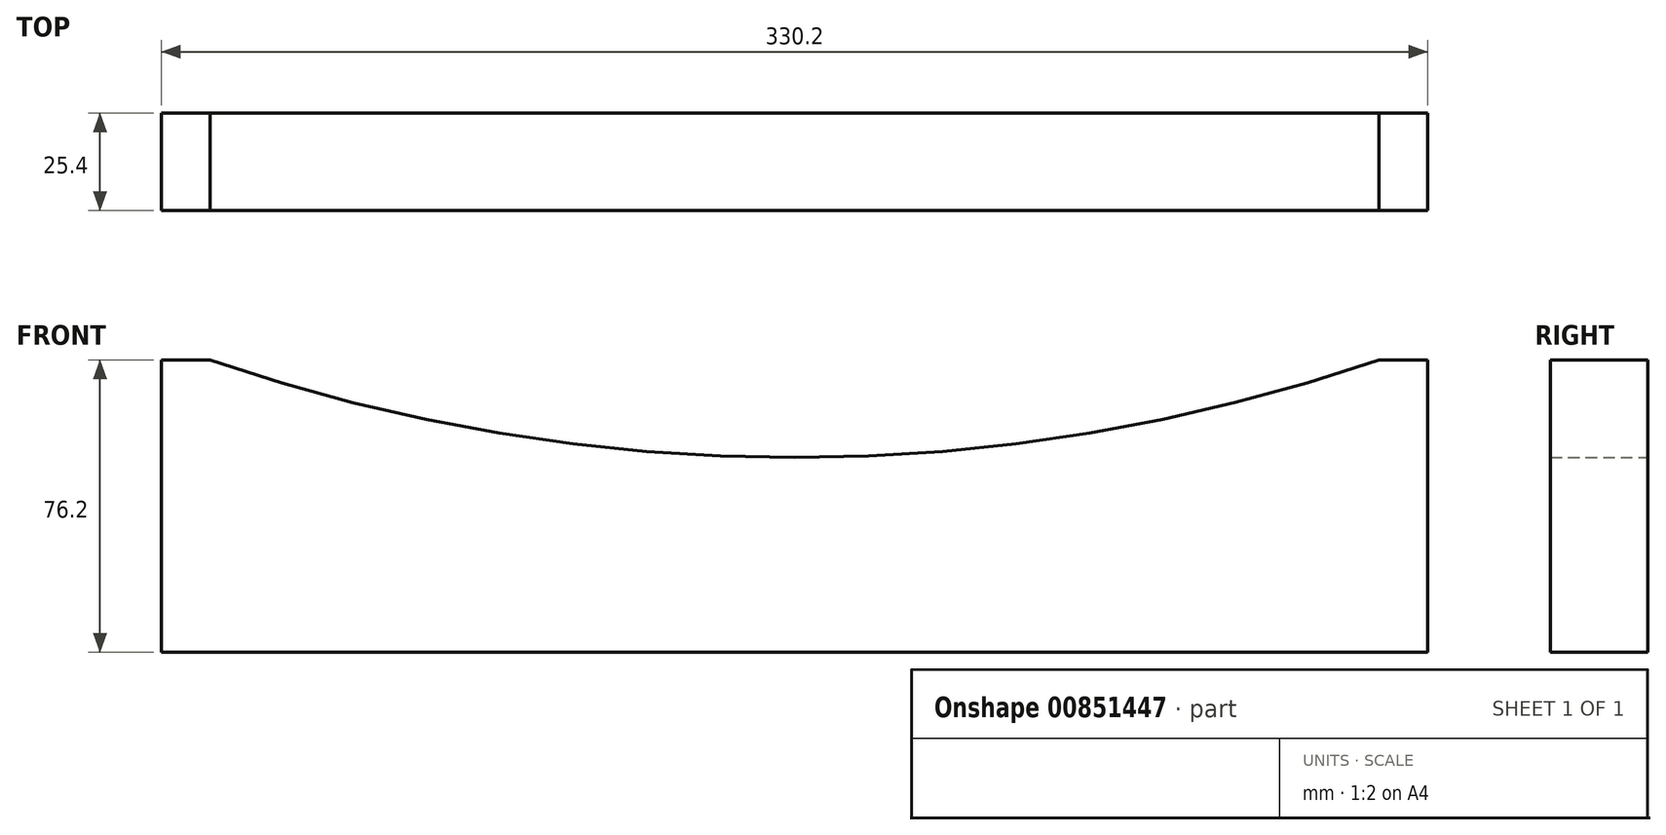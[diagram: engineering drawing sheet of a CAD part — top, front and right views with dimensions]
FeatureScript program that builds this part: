
annotation { "Feature Type Name" : "Feature", "Feature Type Description" : "" }
export const myFeature = defineFeature(function(context is Context, id is Id, definition is map)
    precondition{}
    {
        {
            var Q0;
            Q0=qCreatedBy(makeId("Front.planeOp"),FACE);
            var sketch = newSketch(context, id + "F0", { "sketchPlane" : qUnion([Q0])});
            skLineSegment(sketch, "E0.bottom", {"start": v(-152.21, 56.76) * mm, "end": v(-139.51, 56.76) * mm});
            skLineSegment(sketch, "E0.top", {"start": v(-152.21, -19.44) * mm, "end": v(177.99, -19.44) * mm});
            skLineSegment(sketch, "E0.left", {"start": v(-152.21, 56.76) * mm, "end": v(-152.21, -19.44) * mm});
            skLineSegment(sketch, "E0.right", {"start": v(177.99, 56.76) * mm, "end": v(177.99, -19.44) * mm});
            skArc(sketch, "E1", {"start": v(-139.51, 56.76) * mm, "mid": v(12.89, 31.36) * mm, "end": v(165.29, 56.76) * mm});
            skLineSegment(sketch, "E2.trimOffspring", {"start": v(165.29, 56.76) * mm, "end": v(177.99, 56.76) * mm});
            skSolve(sketch);
        }
        {
            var Q0;
            Q0=makeQuery(id+"F0.imprint","IMPRINT",FACE,{"disambiguationData":[TD([[makeQuery(id+"F0.imprint","IMPRINT",EDGE,{"derivedFrom":sQuery(id+"F0.wireOp",EDGE,"E0.bottom")}),-1.0]])]});
            extrude(context, id + "F1", {"entities" : qUnion([Q0]), "depth" : 25.4 * mm, "offsetDistance" : 25.4 * mm});
        }
    });
